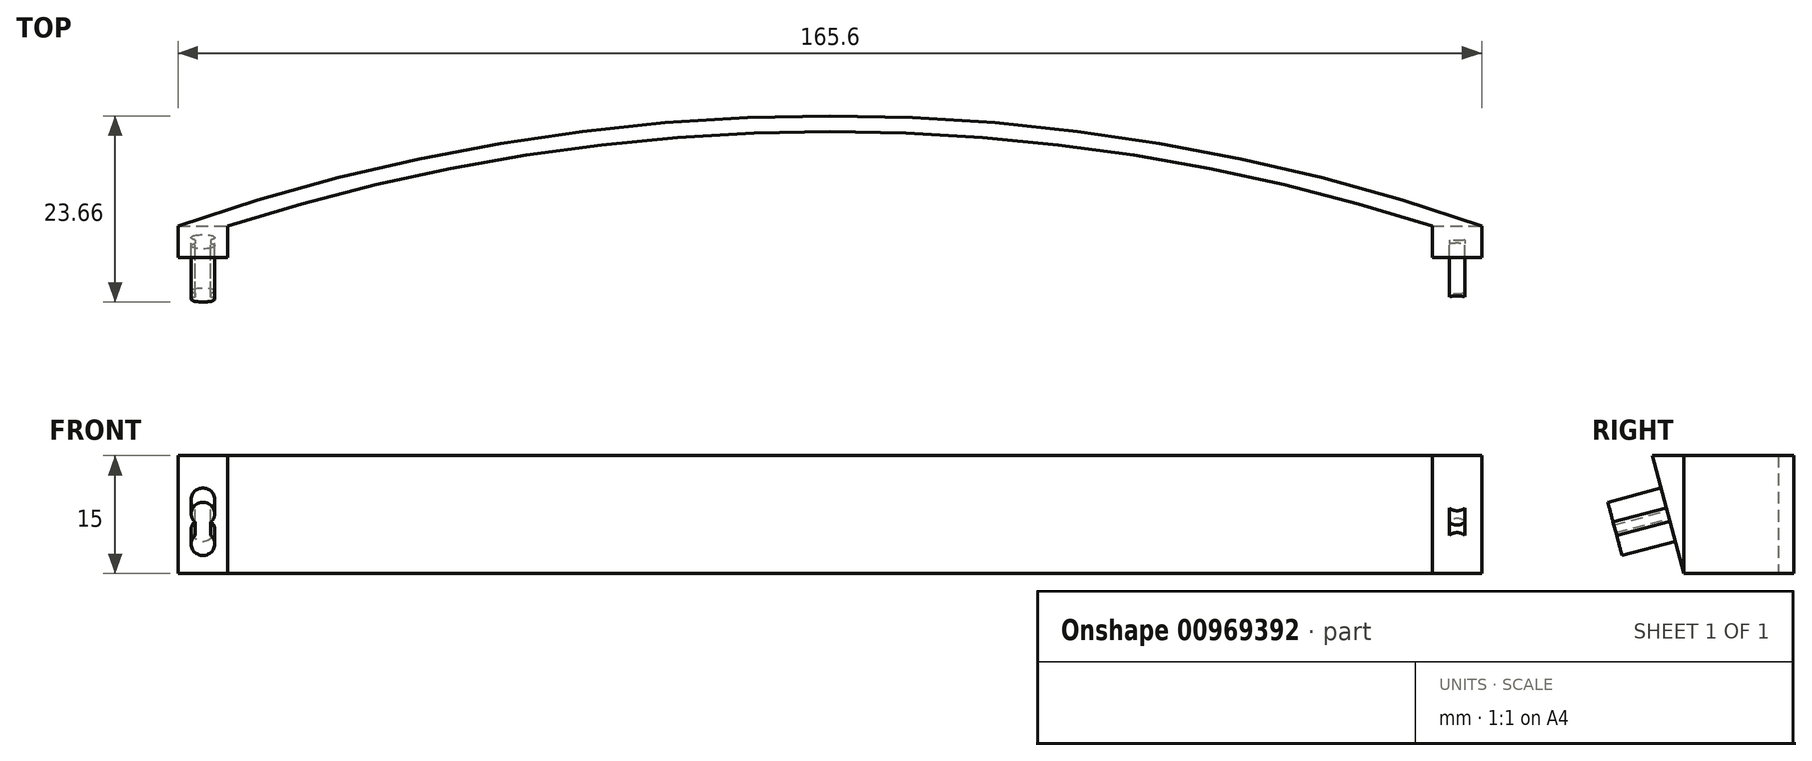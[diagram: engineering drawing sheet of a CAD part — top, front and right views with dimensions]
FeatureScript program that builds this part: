
annotation { "Feature Type Name" : "Feature", "Feature Type Description" : "" }
export const myFeature = defineFeature(function(context is Context, id is Id, definition is map)
    precondition{}
    {
        {
            var Q0;
            Q0=qCreatedBy(makeId("Top.planeOp"),FACE);
            var sketch = newSketch(context, id + "F0", { "sketchPlane" : qUnion([Q0])});
            skLineSegment(sketch, "E0", {"start": v(0, 0) * mm, "end": v(0, -250) * mm, "construction": true});
            skCircle(sketch, "E1", {"center": v(0, -250) * mm, "radius": 250 * mm});
            skLineSegment(sketch, "E2", {"start": v(-76.5, -12) * mm, "end": v(76.5, -12) * mm});
            skCircle(sketch, "E3", {"center": v(0, -250) * mm, "radius": 252 * mm});
            skLineSegment(sketch, "E4", {"start": v(76.5, -12) * mm, "end": v(82.8, -12) * mm});
            skLineSegment(sketch, "E5", {"start": v(-76.5, -12) * mm, "end": v(-82.8, -12) * mm});
            skSolve(sketch);
        }
        {
            var Q0;
            {var subQ3=sQuery(id+"F0.wireOp",EDGE,"E4");Q0=makeQuery(id+"F0.imprint","IMPRINT",FACE,{"disambiguationData":[TD([[makeQuery(id+"F0.imprint","IMPRINT",EDGE,{"derivedFrom":subQ3}),1.0]])]});}
            extrude(context, id + "F1", {"entities" : qUnion([Q0]), "depth" : 15 * mm, "offsetDistance" : 25 * mm});
        }
        {
            var Q0;
            Q0=makeQuery(id+"F1.opExtrude","SWEPT_FACE",FACE,{"disambiguationData":[OSD([sQuery(id+"F0.wireOp",EDGE,"E5")])]});
            var Q1;
            Q1=makeQuery(id+"F1.opExtrude","SWEPT_FACE",FACE,{"disambiguationData":[OSD([sQuery(id+"F0.wireOp",EDGE,"E4")])]});
            extrude(context, id + "F2", {"entities" : qUnion([Q0, Q1]), "operationType" : NewBodyOperationType.ADD, "depth" : 4 * mm, "offsetDistance" : 25 * mm});
        }
        {
            var Q0;
            Q0=makeQuery(id+"F2.opExtrude","SWEPT_FACE",FACE,{"disambiguationData":[OSD([sQuery(id+"F0.wireOp",EDGE,"E3"),sQuery(id+"F0.wireOp",EDGE,"E4")])]});
            var sketch = newSketch(context, id + "F3", { "sketchPlane" : qUnion([Q0])});
            skLineSegment(sketch, "E6", {"start": v(-16, 15) * mm, "end": v(-12, 0) * mm});
            skSolve(sketch);
        }
        {
            var Q0;
            Q0=makeQuery(id+"F3.imprint","IMPRINT",FACE,{"disambiguationData":[TD([[makeQuery(id+"F3.imprint","IMPRINT",EDGE,{"derivedFrom":sQuery(id+"F3.wireOp",EDGE,"E6")}),-1.0]])]});
            extrude(context, id + "F4", {"entities" : qUnion([Q0]), "operationType" : NewBodyOperationType.REMOVE, "oppositeDirection" : true, "depth" : 250 * mm, "offsetDistance" : 25 * mm});
        }
        {
            var Q0;
            {var subQ0=sQuery(id+"F0.wireOp",EDGE,"E3");var subQ1=sQuery(id+"F0.wireOp",EDGE,"E5");Q0=makeQuery(id+"F4.boolean.opBoolean","COPY",FACE,{"disambiguationData":[TD([makeQuery(id+"F2.opExtrude","SWEPT_FACE",FACE,{"disambiguationData":[OSD([subQ0,subQ1])]})])],"derivedFrom":makeQuery(id+"F4.opExtrude","SWEPT_FACE",FACE,{"disambiguationData":[OSD([sQuery(id+"F3.wireOp",EDGE,"E6")])]})});}
            var sketch = newSketch(context, id + "F5", { "sketchPlane" : qUnion([Q0])});
            skLineSegment(sketch, "E7", {"start": v(-79.65, 18.61) * mm, "end": v(-79.65, 3.09) * mm, "construction": true});
            skPoint(sketch, "E8", {"position": v(-79.65, 10.85) * mm});
            skPoint(sketch, "E9", {"position": v(-79.65, 12.85) * mm});
            skPoint(sketch, "E10", {"position": v(-79.65, 8.85) * mm});
            skCircle(sketch, "E11", {"center": v(-79.65, 8.85) * mm, "radius": 1.5 * mm});
            skCircle(sketch, "E12", {"center": v(-79.65, 12.85) * mm, "radius": 1.5 * mm});
            skLineSegment(sketch, "E13", {"start": v(-78.65, 9.97) * mm, "end": v(-78.65, 11.73) * mm});
            skLineSegment(sketch, "E14", {"start": v(-80.65, 9.97) * mm, "end": v(-80.65, 11.73) * mm});
            skLineSegment(sketch, "E15", {"start": v(0, -18.14) * mm, "end": v(0, 23.03) * mm, "construction": true});
            skLineSegment(sketch, "E16.MirrorCS", {"start": v(78.65, 9.97) * mm, "end": v(78.65, 11.73) * mm});
            skLineSegment(sketch, "E17.MirrorCS", {"start": v(80.65, 9.97) * mm, "end": v(80.65, 11.73) * mm});
            skPoint(sketch, "E18.MirrorP", {"position": v(79.65, 8.85) * mm});
            skCircle(sketch, "E19.MirrorC", {"center": v(79.65, 12.85) * mm, "radius": 1.5 * mm});
            skCircle(sketch, "E20.MirrorC", {"center": v(79.65, 8.85) * mm, "radius": 1.5 * mm});
            skPoint(sketch, "E21.MirrorP", {"position": v(79.65, 10.85) * mm});
            skSolve(sketch);
        }
        {
            var Q0;
            {var subQ0=sQuery(id+"F5.wireOp",EDGE,"E11");var subQ1=makeQuery(id+"F5.imprint","INTERSECT",VERTEX,{"derivedFrom":[subQ0,sQuery(id+"F5.wireOp",EDGE,"E13")]});Q0=makeQuery(id+"F5.imprint","IMPRINT",FACE,{"disambiguationData":[TD([[makeQuery(id+"F5.imprint","IMPRINT",EDGE,{"disambiguationData":[TD([[subQ1,-1.0]])],"derivedFrom":subQ0}),1.0]])]});}
            var Q1;
            {var subQ0=sQuery(id+"F5.wireOp",EDGE,"E13");Q1=makeQuery(id+"F5.imprint","IMPRINT",FACE,{"disambiguationData":[TD([[makeQuery(id+"F5.imprint","IMPRINT",EDGE,{"derivedFrom":subQ0}),1.0]])]});}
            var Q2;
            {var subQ0=sQuery(id+"F5.wireOp",EDGE,"E12");var subQ1=makeQuery(id+"F5.imprint","INTERSECT",VERTEX,{"derivedFrom":[subQ0,sQuery(id+"F5.wireOp",EDGE,"E13")]});Q2=makeQuery(id+"F5.imprint","IMPRINT",FACE,{"disambiguationData":[TD([[makeQuery(id+"F5.imprint","IMPRINT",EDGE,{"disambiguationData":[TD([[subQ1,1.0]])],"derivedFrom":subQ0}),1.0]])]});}
            var Q3;
            {var subQ0=sQuery(id+"F5.wireOp",EDGE,"E20.MirrorC");var subQ1=makeQuery(id+"F5.imprint","INTERSECT",VERTEX,{"derivedFrom":[sQuery(id+"F5.wireOp",EDGE,"E16.MirrorCS"),subQ0]});Q3=makeQuery(id+"F5.imprint","IMPRINT",FACE,{"disambiguationData":[TD([[makeQuery(id+"F5.imprint","IMPRINT",EDGE,{"disambiguationData":[TD([[subQ1,-1.0]])],"derivedFrom":subQ0}),-1.0]])]});}
            var Q4;
            {var subQ0=sQuery(id+"F5.wireOp",EDGE,"E16.MirrorCS");Q4=makeQuery(id+"F5.imprint","IMPRINT",FACE,{"disambiguationData":[TD([[makeQuery(id+"F5.imprint","IMPRINT",EDGE,{"derivedFrom":subQ0}),-1.0]])]});}
            var Q5;
            {var subQ0=sQuery(id+"F5.wireOp",EDGE,"E19.MirrorC");var subQ1=makeQuery(id+"F5.imprint","INTERSECT",VERTEX,{"derivedFrom":[sQuery(id+"F5.wireOp",EDGE,"E16.MirrorCS"),subQ0]});Q5=makeQuery(id+"F5.imprint","IMPRINT",FACE,{"disambiguationData":[TD([[makeQuery(id+"F5.imprint","IMPRINT",EDGE,{"disambiguationData":[TD([[subQ1,1.0]])],"derivedFrom":subQ0}),-1.0]])]});}
            extrude(context, id + "F6", {"entities" : qUnion([Q0, Q1, Q2, Q3, Q4, Q5]), "operationType" : NewBodyOperationType.ADD, "depth" : 7 * mm, "offsetDistance" : 25 * mm});
        }
    });
